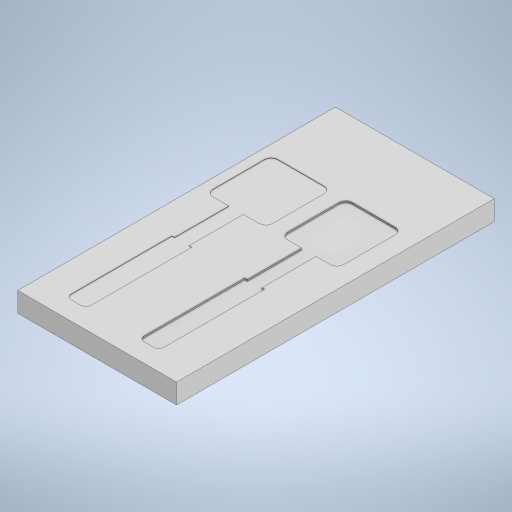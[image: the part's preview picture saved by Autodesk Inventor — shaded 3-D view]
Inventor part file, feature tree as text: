
AUTODESK INVENTOR PART (.ipt)
format: ipt  version: 2024.2 (Build 282272000, 272)  size: 314,880 bytes
history: native  units: in
note: dims shown in document units (in); Inventor stores cm internally (conversion verified against a paired STEP export)
features: extrude x3, sketch x3
ambient origin geometry x8: Origin, YZ Plane, XZ Plane, XY Plane, X Axis, Y Axis, Z Axis, Center Point
bodies: Solid1 (feature_tree)
feature tree (6):
  extrude  "Extrusion1"  Depth=6.0in
  extrude  "Extrusion2"  Depth=0.01in TaperAngle=0.0deg
  extrude  "Extrusion3"  Depth=0.0938in
  sketch  "Sketch1"  dims[d0=3.0in d1=6.0in]
  sketch  "Sketch2"  dims[d2=0.375in d3=0.0in d8=0.01in d9=0.0in]
  sketch  "Sketch3"  dims[d12=0.375in d13=0.0938in d14=0.035in d15=0.0in d22=0.0in d28=0.0in d33=0.0in d34=0.125in d36=1.025in d37=2.0in d40=1.025in d41=0.375in d42=0.0in d43=0.0in d45=0.275in d47=0.0938in]
